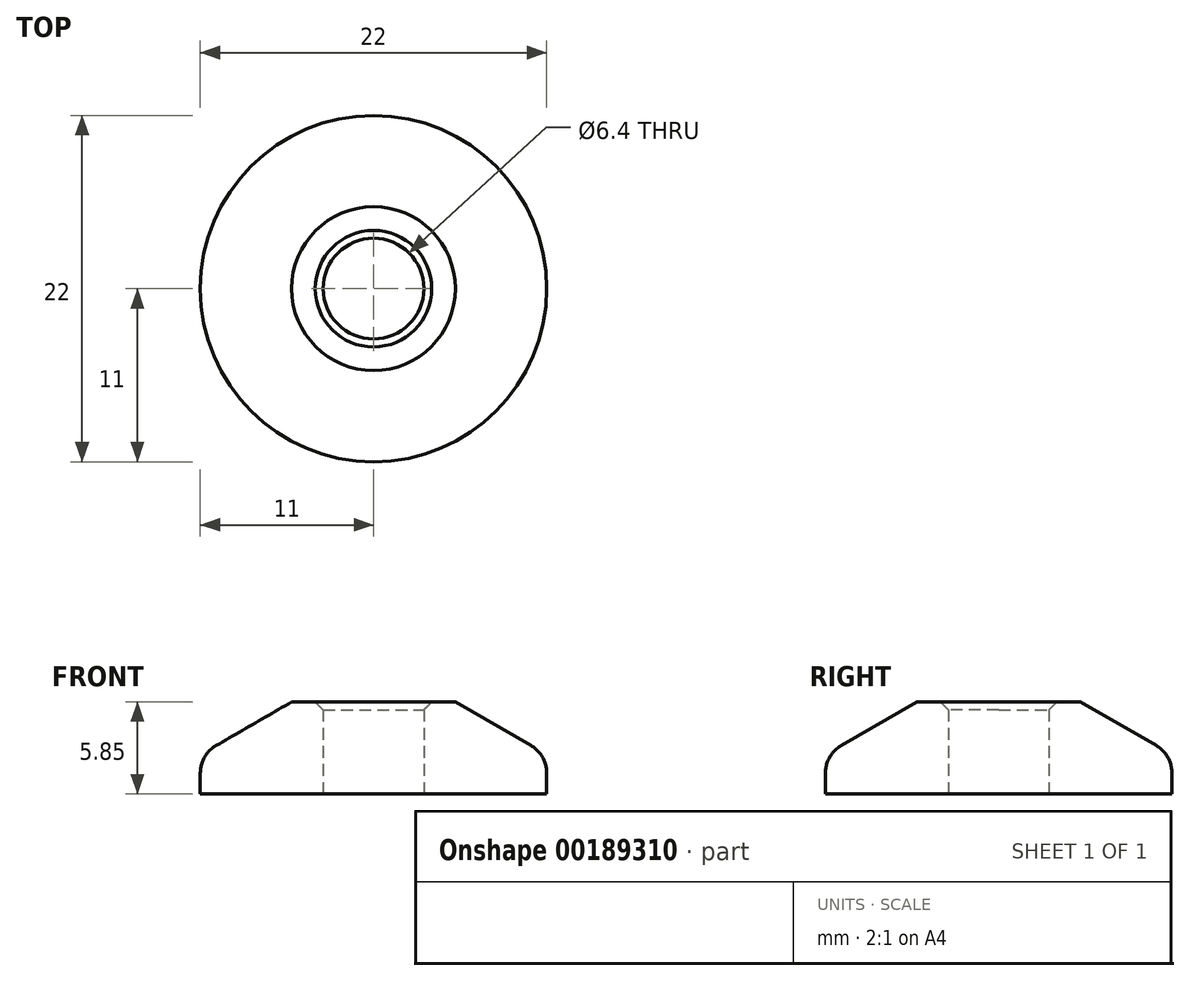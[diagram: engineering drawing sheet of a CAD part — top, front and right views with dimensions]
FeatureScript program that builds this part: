
annotation { "Feature Type Name" : "Feature", "Feature Type Description" : "" }
export const myFeature = defineFeature(function(context is Context, id is Id, definition is map)
    precondition{}
    {
        {
            var Q0;
            Q0=qCreatedBy(makeId("Front.planeOp"),FACE);
            var sketch = newSketch(context, id + "F0", { "sketchPlane" : qUnion([Q0])});
            skLineSegment(sketch, "E0", {"start": v(-3.2, 0) * mm, "end": v(-11, 0) * mm});
            skLineSegment(sketch, "E1", {"start": v(-11, 0) * mm, "end": v(-11, 2.5) * mm});
            skLineSegment(sketch, "E2", {"start": v(-5.2, 5.85) * mm, "end": v(-3.2, 5.85) * mm});
            skLineSegment(sketch, "E3", {"start": v(-3.2, 5.85) * mm, "end": v(-3.2, 0) * mm});
            skLineSegment(sketch, "E4", {"start": v(-11, 2.5) * mm, "end": v(-5.2, 5.85) * mm});
            skLineSegment(sketch, "E5", {"start": v(0, 0) * mm, "end": v(0, 27.17) * mm, "construction": true});
            skSolve(sketch);
        }
        {
            var Q0;
            Q0 = qSketchRegion(id + "F0", true);
            var Q1;
            Q1=sQuery(id+"F0.wireOp",EDGE,"E5");
            revolve(context, id + "F1", {"entities" : qUnion([Q0]), "axis" : qUnion([Q1]), "revolveType" : RevolveType.FULL});
        }
        {
            var Q0;
            Q0=makeQuery(id+"F1.opRevolve","SWEPT_EDGE",EDGE,{"disambiguationData":[OSD([sQuery(id+"F0.wireOp",EDGE,"E1"),sQuery(id+"F0.wireOp",EDGE,"E4")])]});
            fillet(context, id + "F2", {"entities" : qUnion([Q0]), "radius" : 2 * mm, "tangentPropagation" : true, "allowEdgeOverflow" : false});
        }
        {
            var Q0;
            Q0=makeQuery(id+"F1.opRevolve","SWEPT_EDGE",EDGE,{"disambiguationData":[OSD([sQuery(id+"F0.wireOp",EDGE,"E2"),sQuery(id+"F0.wireOp",EDGE,"E3")])]});
            chamfer(context, id + "F3", {"entities" : qUnion([Q0]), "width" : .5 * mm, "tangentPropagation" : true});
        }
    });
